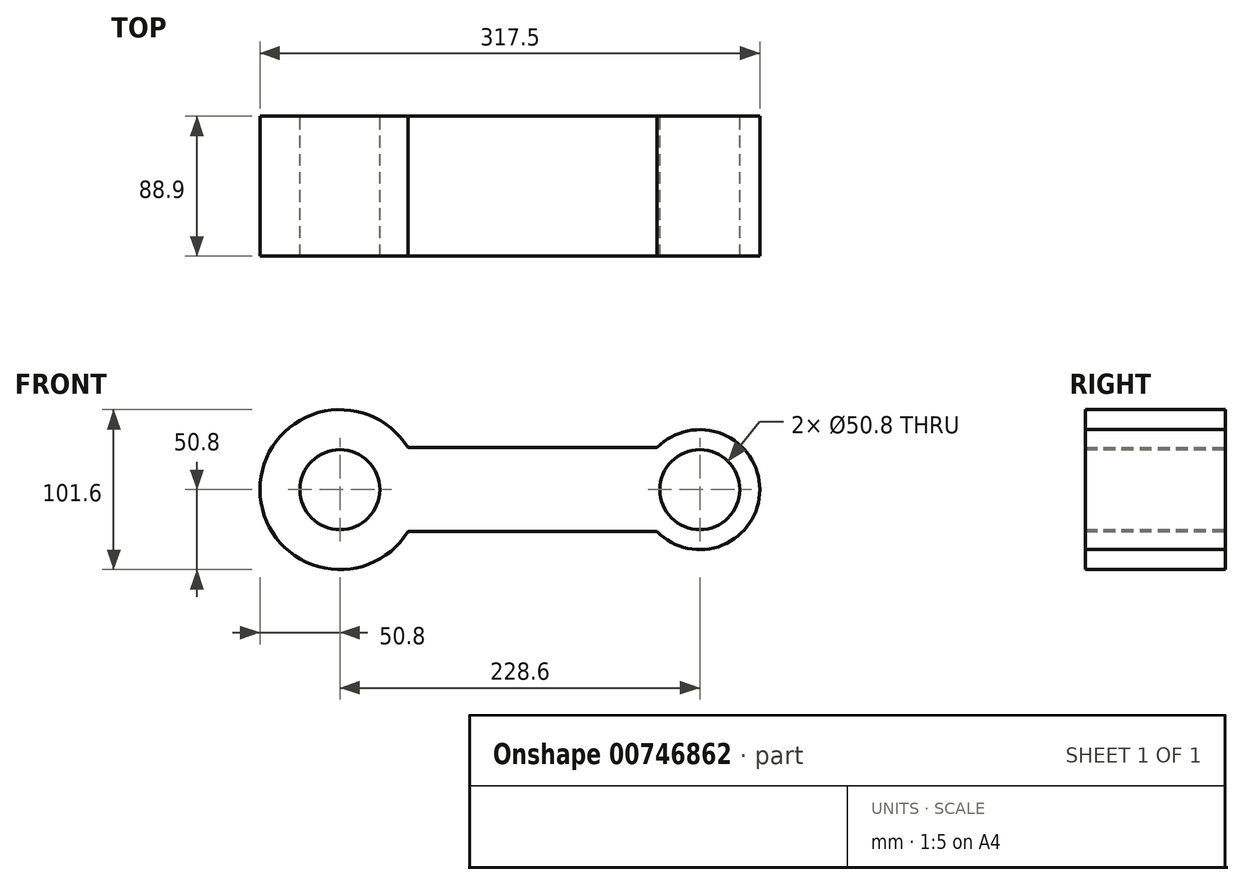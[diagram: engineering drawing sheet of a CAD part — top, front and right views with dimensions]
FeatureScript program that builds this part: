
annotation { "Feature Type Name" : "Feature", "Feature Type Description" : "" }
export const myFeature = defineFeature(function(context is Context, id is Id, definition is map)
    precondition{}
    {
        {
            var Q0;
            Q0=qCreatedBy(makeId("Front.planeOp"),FACE);
            var sketch = newSketch(context, id + "F0", { "sketchPlane" : qUnion([Q0])});
            skCircle(sketch, "E0", {"center": v(0, 0) * mm, "radius": 50.8 * mm});
            skCircle(sketch, "E1", {"center": v(228.6, 0) * mm, "radius": 38.1 * mm});
            skLineSegment(sketch, "E2", {"start": v(0, 0) * mm, "end": v(228.6, 0) * mm, "construction": true});
            skLineSegment(sketch, "E3", {"start": v(43.24, 26.67) * mm, "end": v(201.4, 26.67) * mm});
            skLineSegment(sketch, "E4.MirrorCS", {"start": v(43.24, -26.67) * mm, "end": v(201.4, -26.67) * mm});
            skCircle(sketch, "E5", {"center": v(0, 0) * mm, "radius": 25.4 * mm});
            skCircle(sketch, "E6", {"center": v(228.6, 0) * mm, "radius": 25.4 * mm});
            skSolve(sketch);
        }
        {
            var Q0;
            Q0=makeQuery(id+"F0.imprint","IMPRINT",FACE,{"disambiguationData":[TD([[makeQuery(id+"F0.imprint","IMPRINT",EDGE,{"derivedFrom":sQuery(id+"F0.wireOp",EDGE,"E5")}),-1.0]])]});
            var Q1;
            {var subQ0=sQuery(id+"F0.wireOp",EDGE,"E3");Q1=makeQuery(id+"F0.imprint","IMPRINT",FACE,{"disambiguationData":[TD([[makeQuery(id+"F0.imprint","IMPRINT",EDGE,{"derivedFrom":subQ0}),-1.0]])]});}
            var Q2;
            Q2=makeQuery(id+"F0.imprint","IMPRINT",FACE,{"disambiguationData":[TD([[makeQuery(id+"F0.imprint","IMPRINT",EDGE,{"derivedFrom":sQuery(id+"F0.wireOp",EDGE,"E6")}),-1.0]])]});
            extrude(context, id + "F1", {"entities" : qUnion([Q0, Q1, Q2]), "depth" : 88.9 * mm, "offsetDistance" : 25.4 * mm});
        }
    });
